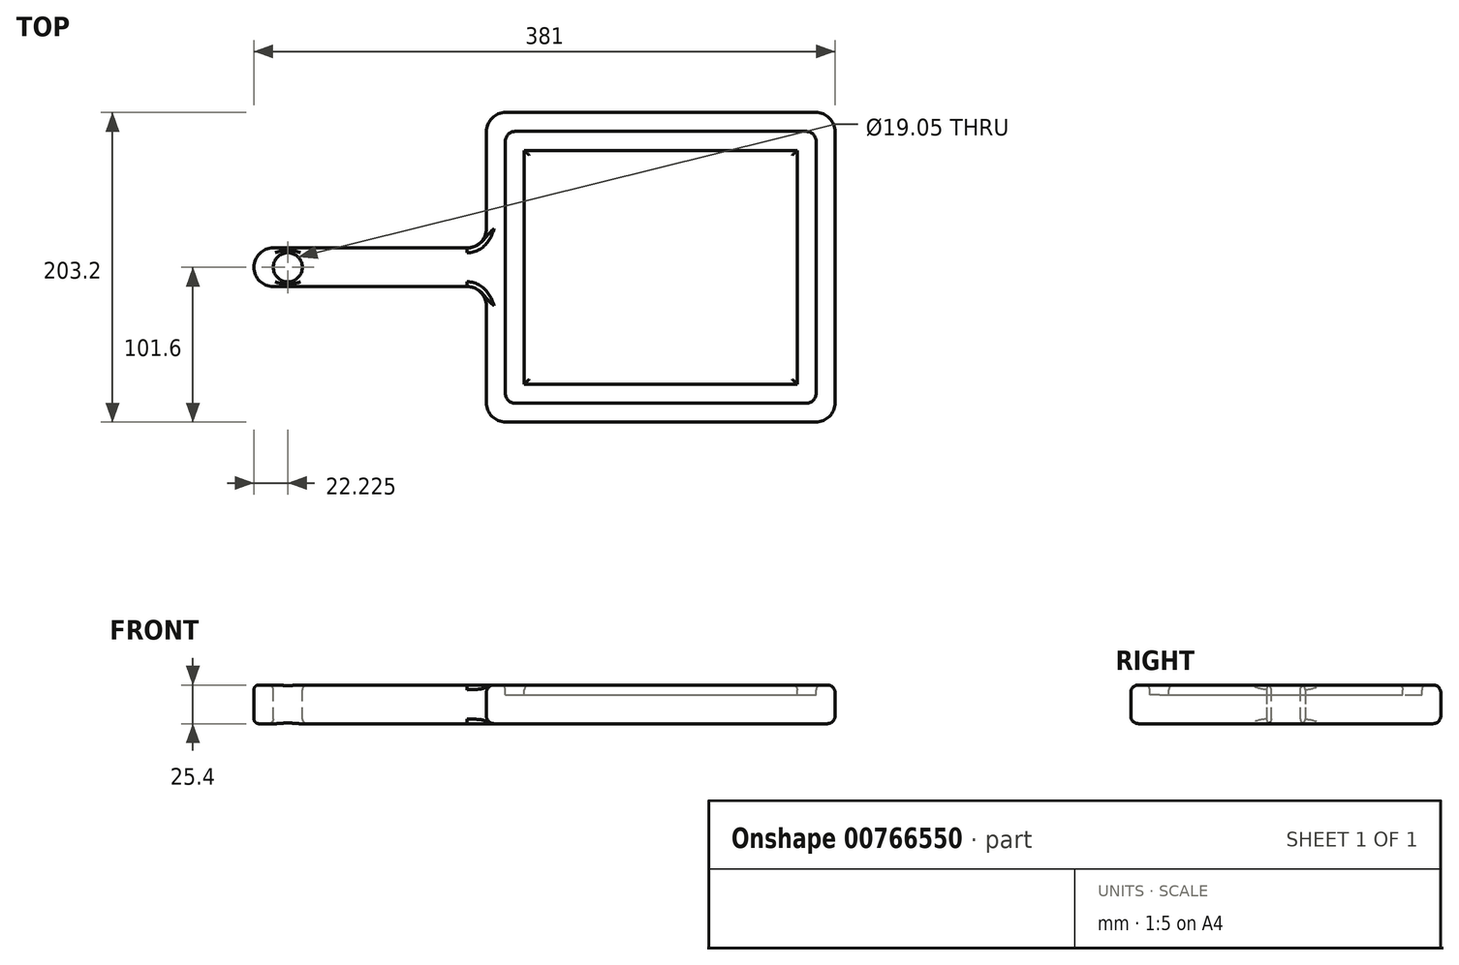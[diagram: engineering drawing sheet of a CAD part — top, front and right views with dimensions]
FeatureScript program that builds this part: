
annotation { "Feature Type Name" : "Feature", "Feature Type Description" : "" }
export const myFeature = defineFeature(function(context is Context, id is Id, definition is map)
    precondition{}
    {
        {
            var Q0;
            Q0=qCreatedBy(makeId("Top.planeOp"),FACE);
            var sketch = newSketch(context, id + "F0", { "sketchPlane" : qUnion([Q0])});
            skLineSegment(sketch, "E0.bottom", {"start": v(0, 0) * mm, "end": v(228.6, 0) * mm});
            skLineSegment(sketch, "E0.top", {"start": v(0, 203.2) * mm, "end": v(228.6, 203.2) * mm});
            skLineSegment(sketch, "E0.left", {"start": v(0, 0) * mm, "end": v(0, 203.2) * mm});
            skLineSegment(sketch, "E0.right", {"start": v(228.6, 0) * mm, "end": v(228.6, 203.2) * mm});
            skLineSegment(sketch, "E1.bottom", {"start": v(0, 88.9) * mm, "end": v(-152.4, 88.9) * mm});
            skLineSegment(sketch, "E1.top", {"start": v(0, 114.3) * mm, "end": v(-152.4, 114.3) * mm});
            skLineSegment(sketch, "E1.left", {"start": v(0, 88.9) * mm, "end": v(0, 114.3) * mm});
            skLineSegment(sketch, "E1.right", {"start": v(-152.4, 88.9) * mm, "end": v(-152.4, 114.3) * mm});
            skSolve(sketch);
        }
        {
            var Q0;
            {var subQ3=sQuery(id+"F0.wireOp",EDGE,"E0.bottom");Q0=makeQuery(id+"F0.imprint","IMPRINT",FACE,{"disambiguationData":[TD([[makeQuery(id+"F0.imprint","IMPRINT",EDGE,{"derivedFrom":subQ3}),1.0]])]});}
            var Q1;
            Q1=makeQuery(id+"F0.imprint","IMPRINT",FACE,{"disambiguationData":[TD([[makeQuery(id+"F0.imprint","IMPRINT",EDGE,{"derivedFrom":sQuery(id+"F0.wireOp",EDGE,"E1.bottom")}),-1.0]])]});
            extrude(context, id + "F1", {"entities" : qUnion([Q0, Q1]), "depth" : 25.4 * mm, "offsetDistance" : 25.4 * mm});
        }
        {
            var Q0;
            Q0=makeQuery(id+"F1.opExtrude","CAP_FACE",FACE,{"disambiguationData":[OSD([sQuery(id+"F0.wireOp",EDGE,"E0.bottom"),sQuery(id+"F0.wireOp",EDGE,"E0.top"),sQuery(id+"F0.wireOp",EDGE,"E0.left"),sQuery(id+"F0.wireOp",EDGE,"E0.right"),sQuery(id+"F0.wireOp",EDGE,"E1.bottom"),sQuery(id+"F0.wireOp",EDGE,"E1.top"),sQuery(id+"F0.wireOp",EDGE,"E1.right")])],"isStart":false});
            var sketch = newSketch(context, id + "F2", { "sketchPlane" : qUnion([Q0])});
            skPoint(sketch, "E2.centerSnap0", {"position": v(-152.4, 101.6) * mm});
            skCircle(sketch, "E3", {"center": v(-130.18, 101.6) * mm, "radius": 9.53 * mm});
            skSolve(sketch);
        }
        {
            var Q0;
            Q0 = qSketchRegion(id + "F2", true);
            extrude(context, id + "F3", {"entities" : qUnion([Q0]), "operationType" : NewBodyOperationType.REMOVE, "oppositeDirection" : true, "depth" : 25.4 * mm, "offsetDistance" : 25.4 * mm});
        }
        {
            var Q0;
            Q0=makeQuery(id+"F1.opExtrude","CAP_FACE",FACE,{"disambiguationData":[OSD([sQuery(id+"F0.wireOp",EDGE,"E0.bottom"),sQuery(id+"F0.wireOp",EDGE,"E0.top"),sQuery(id+"F0.wireOp",EDGE,"E0.left"),sQuery(id+"F0.wireOp",EDGE,"E0.right"),sQuery(id+"F0.wireOp",EDGE,"E1.bottom"),sQuery(id+"F0.wireOp",EDGE,"E1.top"),sQuery(id+"F0.wireOp",EDGE,"E1.right")])],"isStart":false});
            var sketch = newSketch(context, id + "F4", { "sketchPlane" : qUnion([Q0])});
            skLineSegment(sketch, "E4.0", {"start": v(12.45, 12.45) * mm, "end": v(12.45, 88.9) * mm});
            skLineSegment(sketch, "E4.1", {"start": v(12.45, 114.3) * mm, "end": v(12.45, 190.75) * mm});
            skLineSegment(sketch, "E4.2", {"start": v(12.45, 190.75) * mm, "end": v(216.15, 190.75) * mm});
            skLineSegment(sketch, "E4.3", {"start": v(216.15, 12.45) * mm, "end": v(216.15, 190.75) * mm});
            skLineSegment(sketch, "E4.4", {"start": v(12.45, 12.45) * mm, "end": v(216.15, 12.45) * mm});
            skLineSegment(sketch, "E5", {"start": v(12.45, 114.3) * mm, "end": v(12.45, 88.9) * mm});
            skLineSegment(sketch, "E6.0", {"start": v(24.9, 114.3) * mm, "end": v(24.9, 178.3) * mm});
            skLineSegment(sketch, "E6.1", {"start": v(203.7, 24.9) * mm, "end": v(203.7, 178.3) * mm});
            skLineSegment(sketch, "E6.2", {"start": v(24.9, 24.9) * mm, "end": v(203.7, 24.9) * mm});
            skLineSegment(sketch, "E6.3", {"start": v(24.9, 178.3) * mm, "end": v(203.7, 178.3) * mm});
            skLineSegment(sketch, "E6.4", {"start": v(24.9, 24.9) * mm, "end": v(24.9, 88.9) * mm});
            skLineSegment(sketch, "E6.5", {"start": v(24.9, 114.3) * mm, "end": v(24.9, 88.9) * mm});
            skSolve(sketch);
        }
        {
            var Q0;
            Q0=makeQuery(id+"F4.imprint","IMPRINT",FACE,{"disambiguationData":[TD([[makeQuery(id+"F4.imprint","IMPRINT",EDGE,{"derivedFrom":sQuery(id+"F4.wireOp",EDGE,"E4.0")}),-1.0]])]});
            extrude(context, id + "F5", {"entities" : qUnion([Q0]), "operationType" : NewBodyOperationType.REMOVE, "oppositeDirection" : true, "depth" : 6.35 * mm, "offsetDistance" : 25.4 * mm});
        }
        {
            var Q0;
            Q0=makeQuery(id+"F5.boolean.opBoolean","COPY",EDGE,{"derivedFrom":makeQuery(id+"F5.opExtrude","SWEPT_EDGE",EDGE,{"disambiguationData":[OSD([sQuery(id+"F4.wireOp",EDGE,"E4.1"),sQuery(id+"F4.wireOp",EDGE,"E4.2")])]})});
            var Q1;
            Q1=makeQuery(id+"F5.boolean.opBoolean","COPY",EDGE,{"derivedFrom":makeQuery(id+"F5.opExtrude","SWEPT_EDGE",EDGE,{"disambiguationData":[OSD([sQuery(id+"F4.wireOp",EDGE,"E4.2"),sQuery(id+"F4.wireOp",EDGE,"E4.3")])]})});
            var Q2;
            Q2=makeQuery(id+"F5.boolean.opBoolean","COPY",EDGE,{"derivedFrom":makeQuery(id+"F5.opExtrude","SWEPT_EDGE",EDGE,{"disambiguationData":[OSD([sQuery(id+"F4.wireOp",EDGE,"E4.3"),sQuery(id+"F4.wireOp",EDGE,"E4.4")])]})});
            var Q3;
            Q3=makeQuery(id+"F5.boolean.opBoolean","COPY",EDGE,{"derivedFrom":makeQuery(id+"F5.opExtrude","SWEPT_EDGE",EDGE,{"disambiguationData":[OSD([sQuery(id+"F4.wireOp",EDGE,"E4.0"),sQuery(id+"F4.wireOp",EDGE,"E4.4")])]})});
            fillet(context, id + "F6", {"entities" : qUnion([Q0, Q1, Q2, Q3]), "radius" : 6.35 * mm, "tangentPropagation" : true, "allowEdgeOverflow" : false});
        }
        {
            var Q0;
            Q0=makeQuery(id+"F1.opExtrude","SWEPT_EDGE",EDGE,{"disambiguationData":[OSD([sQuery(id+"F0.wireOp",EDGE,"E0.bottom"),sQuery(id+"F0.wireOp",EDGE,"E0.right")])]});
            var Q1;
            Q1=makeQuery(id+"F1.opExtrude","SWEPT_EDGE",EDGE,{"disambiguationData":[OSD([sQuery(id+"F0.wireOp",EDGE,"E0.top"),sQuery(id+"F0.wireOp",EDGE,"E0.right")])]});
            fillet(context, id + "F7", {"entities" : qUnion([Q0, Q1]), "radius" : 12.7 * mm, "tangentPropagation" : true, "allowEdgeOverflow" : false});
        }
        {
            var Q0;
            Q0=makeQuery(id+"F1.opExtrude","SWEPT_EDGE",EDGE,{"disambiguationData":[OSD([sQuery(id+"F0.wireOp",EDGE,"E0.bottom"),sQuery(id+"F0.wireOp",EDGE,"E0.left")])]});
            var Q1;
            Q1=makeQuery(id+"F1.opExtrude","SWEPT_EDGE",EDGE,{"disambiguationData":[OSD([sQuery(id+"F0.wireOp",EDGE,"E0.top"),sQuery(id+"F0.wireOp",EDGE,"E0.left")])]});
            fillet(context, id + "F8", {"entities" : qUnion([Q0, Q1]), "radius" : 12.7 * mm, "tangentPropagation" : true, "allowEdgeOverflow" : false});
        }
        {
            var Q0;
            Q0=makeQuery(id+"F8.opFillet","BLEND_FACE",FACE,{"disambiguationData":[OSD([sQuery(id+"F0.wireOp",EDGE,"E0.top"),sQuery(id+"F0.wireOp",EDGE,"E0.left")])]});
            var Q1;
            {var subQ0=sQuery(id+"F0.wireOp",EDGE,"E1.right");var subQ1=sQuery(id+"F0.wireOp",EDGE,"E1.top");var subQ2=sQuery(id+"F0.wireOp",EDGE,"E1.bottom");var subQ3=sQuery(id+"F0.wireOp",EDGE,"E0.right");var subQ4=sQuery(id+"F0.wireOp",EDGE,"E0.bottom");var subQ5=sQuery(id+"F0.wireOp",EDGE,"E0.left");var subQ6=sQuery(id+"F0.wireOp",EDGE,"E0.top");Q1=makeQuery(id+"F8.opFillet","BLEND_EDGE",EDGE,{"blendedFrom":[makeQuery(id+"F1.opExtrude","SWEPT_EDGE",EDGE,{"disambiguationData":[OSD([subQ4,subQ5])]}),makeQuery(id+"F5.boolean.opBoolean","SPLIT",FACE,{"disambiguationData":[TD([makeQuery(id+"F1.opExtrude","SWEPT_FACE",FACE,{"disambiguationData":[OSD([subQ4])]})])],"derivedFrom":makeQuery(id+"F1.opExtrude","CAP_FACE",FACE,{"disambiguationData":[OSD([subQ4,subQ6,subQ5,subQ3,subQ2,subQ1,subQ0])],"isStart":false})})],"blendedInto":[makeQuery(id+"F5.boolean.opBoolean","SPLIT",FACE,{"disambiguationData":[TD([makeQuery(id+"F1.opExtrude","SWEPT_FACE",FACE,{"disambiguationData":[OSD([subQ4])]})])],"derivedFrom":makeQuery(id+"F1.opExtrude","CAP_FACE",FACE,{"disambiguationData":[OSD([subQ4,subQ6,subQ5,subQ3,subQ2,subQ1,subQ0])],"isStart":false})})]});}
            var Q2;
            {var subQ0=sQuery(id+"F0.wireOp",EDGE,"E1.right");var subQ1=sQuery(id+"F0.wireOp",EDGE,"E1.top");var subQ2=sQuery(id+"F0.wireOp",EDGE,"E1.bottom");var subQ3=sQuery(id+"F0.wireOp",EDGE,"E0.right");var subQ4=sQuery(id+"F0.wireOp",EDGE,"E0.bottom");var subQ5=sQuery(id+"F0.wireOp",EDGE,"E0.left");var subQ6=sQuery(id+"F0.wireOp",EDGE,"E0.top");Q2=makeQuery(id+"F7.opFillet","BLEND_EDGE",EDGE,{"blendedFrom":[makeQuery(id+"F1.opExtrude","SWEPT_EDGE",EDGE,{"disambiguationData":[OSD([subQ6,subQ3])]}),makeQuery(id+"F5.boolean.opBoolean","SPLIT",FACE,{"disambiguationData":[TD([makeQuery(id+"F1.opExtrude","SWEPT_FACE",FACE,{"disambiguationData":[OSD([subQ4])]})])],"derivedFrom":makeQuery(id+"F1.opExtrude","CAP_FACE",FACE,{"disambiguationData":[OSD([subQ4,subQ6,subQ5,subQ3,subQ2,subQ1,subQ0])],"isStart":false})})],"blendedInto":[makeQuery(id+"F5.boolean.opBoolean","SPLIT",FACE,{"disambiguationData":[TD([makeQuery(id+"F1.opExtrude","SWEPT_FACE",FACE,{"disambiguationData":[OSD([subQ4])]})])],"derivedFrom":makeQuery(id+"F1.opExtrude","CAP_FACE",FACE,{"disambiguationData":[OSD([subQ4,subQ6,subQ5,subQ3,subQ2,subQ1,subQ0])],"isStart":false})})]});}
            fillet(context, id + "F9", {"entities" : qUnion([Q0, Q1, Q2]), "radius" : 5.08 * mm, "tangentPropagation" : true, "allowEdgeOverflow" : false});
        }
        {
            var Q0;
            Q0=makeQuery(id+"F1.opExtrude","SWEPT_EDGE",EDGE,{"disambiguationData":[OSD([sQuery(id+"F0.wireOp",EDGE,"E0.left"),sQuery(id+"F0.wireOp",EDGE,"E1.top"),sQuery(id+"F0.wireOp",EDGE,"E1.left")])]});
            var Q1;
            Q1=makeQuery(id+"F1.opExtrude","SWEPT_EDGE",EDGE,{"disambiguationData":[OSD([sQuery(id+"F0.wireOp",EDGE,"E1.top"),sQuery(id+"F0.wireOp",EDGE,"E1.right")])]});
            var Q2;
            Q2=makeQuery(id+"F1.opExtrude","SWEPT_EDGE",EDGE,{"disambiguationData":[OSD([sQuery(id+"F0.wireOp",EDGE,"E0.left"),sQuery(id+"F0.wireOp",EDGE,"E1.bottom"),sQuery(id+"F0.wireOp",EDGE,"E1.left")])]});
            var Q3;
            Q3=makeQuery(id+"F1.opExtrude","SWEPT_EDGE",EDGE,{"disambiguationData":[OSD([sQuery(id+"F0.wireOp",EDGE,"E1.bottom"),sQuery(id+"F0.wireOp",EDGE,"E1.right")])]});
            fillet(context, id + "F10", {"entities" : qUnion([Q0, Q1, Q2, Q3]), "radius" : 12.7 * mm, "tangentPropagation" : true, "allowEdgeOverflow" : false});
        }
        {
            var Q0;
            Q0=makeQuery(id+"F5.boolean.opBoolean","SPLIT",FACE,{"disambiguationData":[TD([makeQuery(id+"F5.opExtrude","SWEPT_FACE",FACE,{"disambiguationData":[OSD([sQuery(id+"F4.wireOp",EDGE,"E6.1")])]})])],"derivedFrom":makeQuery(id+"F1.opExtrude","CAP_FACE",FACE,{"disambiguationData":[OSD([sQuery(id+"F0.wireOp",EDGE,"E0.bottom"),sQuery(id+"F0.wireOp",EDGE,"E0.top"),sQuery(id+"F0.wireOp",EDGE,"E0.left"),sQuery(id+"F0.wireOp",EDGE,"E0.right"),sQuery(id+"F0.wireOp",EDGE,"E1.bottom"),sQuery(id+"F0.wireOp",EDGE,"E1.top"),sQuery(id+"F0.wireOp",EDGE,"E1.right")])],"isStart":false})});
            var Q1;
            Q1=makeQuery(id+"F1.opExtrude","CAP_FACE",FACE,{"disambiguationData":[OSD([sQuery(id+"F0.wireOp",EDGE,"E0.bottom"),sQuery(id+"F0.wireOp",EDGE,"E0.top"),sQuery(id+"F0.wireOp",EDGE,"E0.left"),sQuery(id+"F0.wireOp",EDGE,"E0.right"),sQuery(id+"F0.wireOp",EDGE,"E1.bottom"),sQuery(id+"F0.wireOp",EDGE,"E1.top"),sQuery(id+"F0.wireOp",EDGE,"E1.right")])],"isStart":true});
            var Q2;
            {var subQ0=sQuery(id+"F0.wireOp",EDGE,"E1.right");var subQ1=sQuery(id+"F0.wireOp",EDGE,"E1.top");var subQ2=sQuery(id+"F0.wireOp",EDGE,"E1.bottom");var subQ3=sQuery(id+"F0.wireOp",EDGE,"E0.right");var subQ4=sQuery(id+"F0.wireOp",EDGE,"E0.bottom");var subQ5=sQuery(id+"F0.wireOp",EDGE,"E0.left");var subQ6=sQuery(id+"F0.wireOp",EDGE,"E0.top");Q2=makeQuery(id+"F5.boolean.opBoolean","SPLIT",FACE,{"disambiguationData":[TD([makeQuery(id+"F1.opExtrude","SWEPT_FACE",FACE,{"disambiguationData":[OSD([subQ4])]})])],"derivedFrom":makeQuery(id+"F1.opExtrude","CAP_FACE",FACE,{"disambiguationData":[OSD([subQ4,subQ6,subQ5,subQ3,subQ2,subQ1,subQ0])],"isStart":false})});}
            fillet(context, id + "F11", {"entities" : qUnion([Q0, Q1, Q2]), "radius" : 3.17 * mm, "tangentPropagation" : true, "allowEdgeOverflow" : false});
        }
    });
